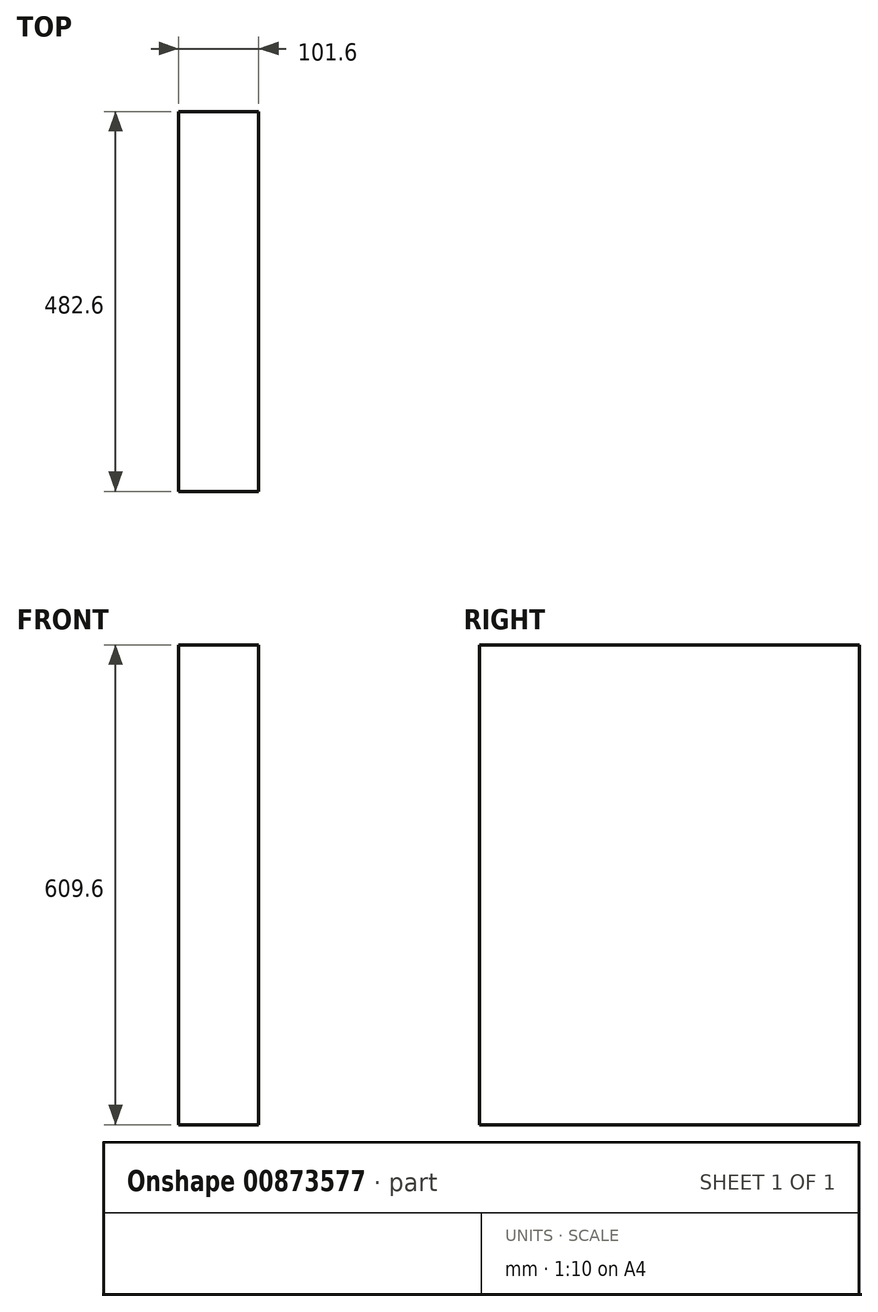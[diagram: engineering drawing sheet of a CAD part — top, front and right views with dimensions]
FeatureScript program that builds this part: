
annotation { "Feature Type Name" : "Feature", "Feature Type Description" : "" }
export const myFeature = defineFeature(function(context is Context, id is Id, definition is map)
    precondition{}
    {
        {
            var Q0;
            Q0=qCreatedBy(makeId("Top.planeOp"),FACE);
            var sketch = newSketch(context, id + "F0", { "sketchPlane" : qUnion([Q0])});
            skLineSegment(sketch, "E0.bottom", {"start": v(0, 0) * mm, "end": v(101.6, 0) * mm});
            skLineSegment(sketch, "E0.top", {"start": v(0, 482.6) * mm, "end": v(101.6, 482.6) * mm});
            skLineSegment(sketch, "E0.left", {"start": v(0, 0) * mm, "end": v(0, 482.6) * mm});
            skLineSegment(sketch, "E0.right", {"start": v(101.6, 0) * mm, "end": v(101.6, 482.6) * mm});
            skSolve(sketch);
        }
        {
            var Q0;
            Q0=makeQuery(id+"F0.imprint","IMPRINT",FACE,{"disambiguationData":[TD([[makeQuery(id+"F0.imprint","IMPRINT",EDGE,{"derivedFrom":sQuery(id+"F0.wireOp",EDGE,"E0.bottom")}),1.0]])]});
            extrude(context, id + "F1", {"entities" : qUnion([Q0]), "depth" : 609.6 * mm, "offsetDistance" : 25.4 * mm});
        }
    });
